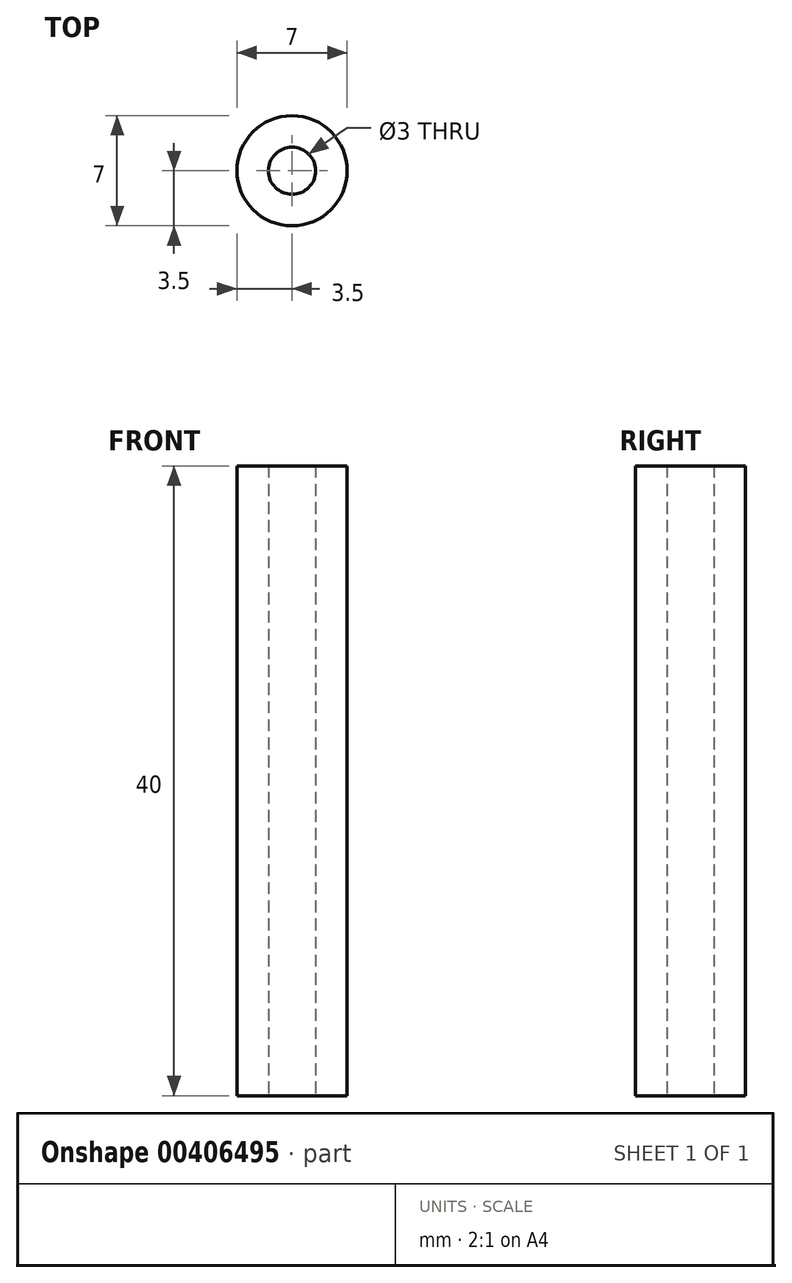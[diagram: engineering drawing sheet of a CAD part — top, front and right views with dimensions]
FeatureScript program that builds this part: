
annotation { "Feature Type Name" : "Feature", "Feature Type Description" : "" }
export const myFeature = defineFeature(function(context is Context, id is Id, definition is map)
    precondition{}
    {
        {
            var Q0;
            Q0=qCreatedBy(makeId("Top.planeOp"),FACE);
            var sketch = newSketch(context, id + "F0", { "sketchPlane" : qUnion([Q0])});
            skCircle(sketch, "E0", {"center": v(0, 0) * mm, "radius": 1.5 * mm});
            skCircle(sketch, "E1", {"center": v(0, 0) * mm, "radius": 3.5 * mm});
            skSolve(sketch);
        }
        {
            var Q0;
            Q0=makeQuery(id+"F0.imprint","IMPRINT",FACE,{"disambiguationData":[TD([[makeQuery(id+"F0.imprint","IMPRINT",EDGE,{"derivedFrom":sQuery(id+"F0.wireOp",EDGE,"E0")}),-1.0]])]});
            extrude(context, id + "F1", {"entities" : qUnion([Q0]), "depth" : 40 * mm});
        }
    });
